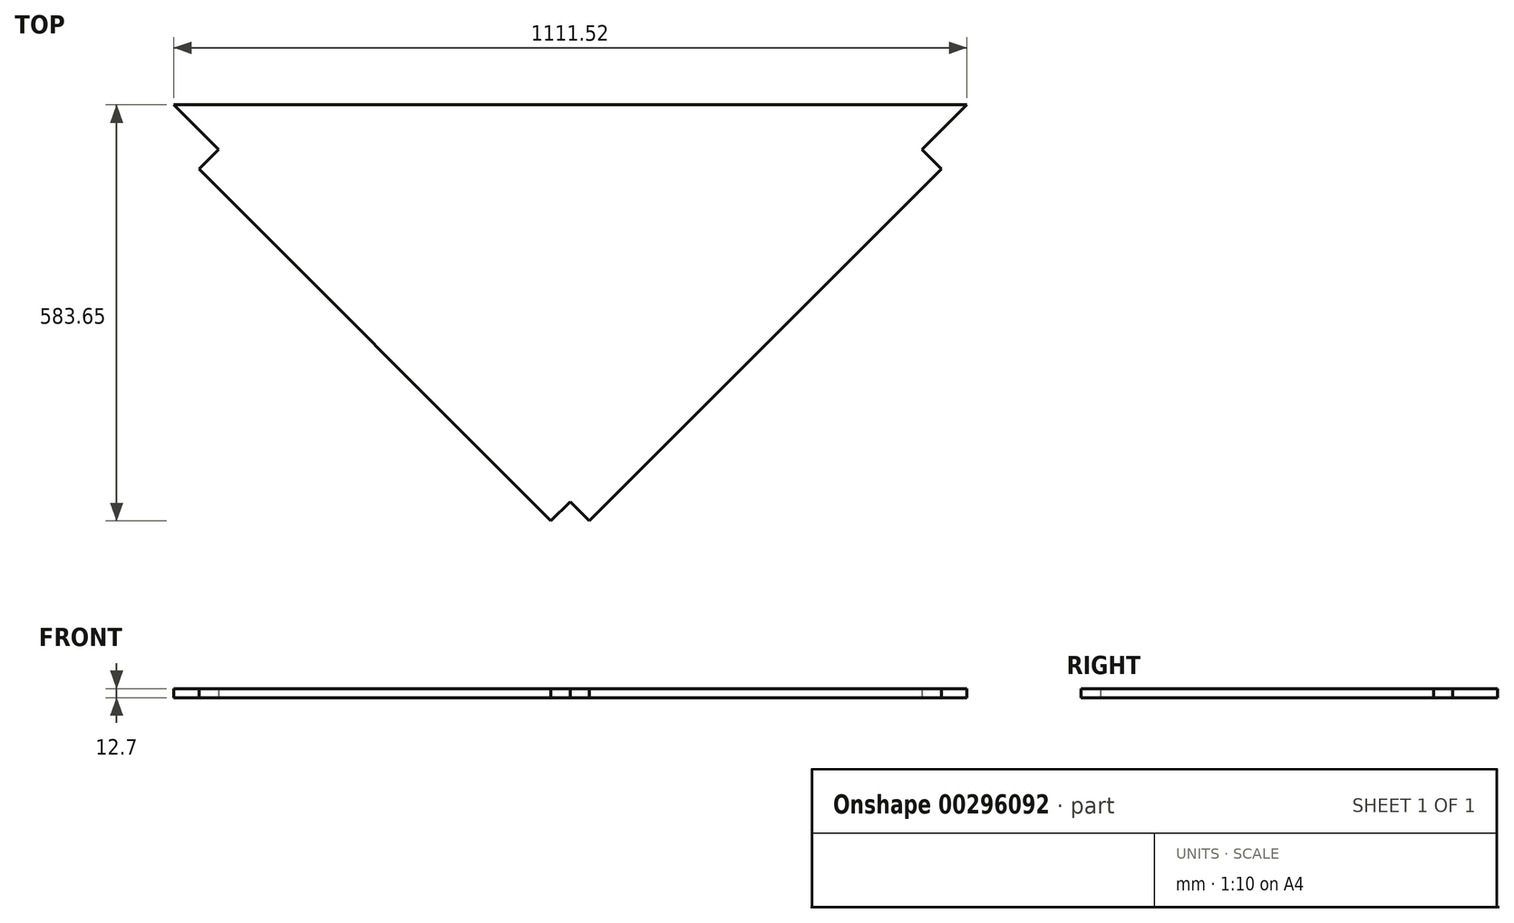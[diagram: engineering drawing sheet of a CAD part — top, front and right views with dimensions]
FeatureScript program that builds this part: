
annotation { "Feature Type Name" : "Feature", "Feature Type Description" : "" }
export const myFeature = defineFeature(function(context is Context, id is Id, definition is map)
    precondition{}
    {
        {
            var Q0;
            Q0=qCreatedBy(makeId("Top.planeOp"),FACE);
            var sketch = newSketch(context, id + "F0", { "sketchPlane" : qUnion([Q0])});
            skLineSegment(sketch, "E0", {"start": v(-555.76, 303.2) * mm, "end": v(555.76, 303.2) * mm});
            skLineSegment(sketch, "E1", {"start": v(519.92, 213.37) * mm, "end": v(26.92, -280.45) * mm});
            skLineSegment(sketch, "E2", {"start": v(-26.96, -280.4) * mm, "end": v(-519.92, 213.37) * mm});
            skLineSegment(sketch, "E3", {"start": v(-519.92, 213.37) * mm, "end": v(-492.96, 240.29) * mm});
            skLineSegment(sketch, "E4", {"start": v(-492.96, 240.29) * mm, "end": v(-555.76, 303.2) * mm});
            skLineSegment(sketch, "E5", {"start": v(519.92, 213.37) * mm, "end": v(492.95, 240.29) * mm});
            skLineSegment(sketch, "E6", {"start": v(492.95, 240.29) * mm, "end": v(555.76, 303.2) * mm});
            skLineSegment(sketch, "E7", {"start": v(-26.96, -280.4) * mm, "end": v(0, -253.49) * mm});
            skLineSegment(sketch, "E8", {"start": v(0, -253.49) * mm, "end": v(26.92, -280.45) * mm});
            skLineSegment(sketch, "E9", {"start": v(-555.76, 303.2) * mm, "end": v(-609.6, 303.2) * mm});
            skLineSegment(sketch, "E10", {"start": v(-519.92, 213.37) * mm, "end": v(-609.6, 303.2) * mm});
            skLineSegment(sketch, "E11", {"start": v(555.76, 303.2) * mm, "end": v(609.6, 303.2) * mm});
            skLineSegment(sketch, "E12", {"start": v(519.92, 213.37) * mm, "end": v(609.6, 303.2) * mm});
            skSolve(sketch);
        }
        {
            var Q0;
            Q0=makeQuery(id+"F0.imprint","IMPRINT",FACE,{"disambiguationData":[TD([[makeQuery(id+"F0.imprint","IMPRINT",EDGE,{"derivedFrom":sQuery(id+"F0.wireOp",EDGE,"E0")}),-1.0]])]});
            extrude(context, id + "F1", {"entities" : qUnion([Q0]), "depth" : 12.7 * mm});
        }
    });
